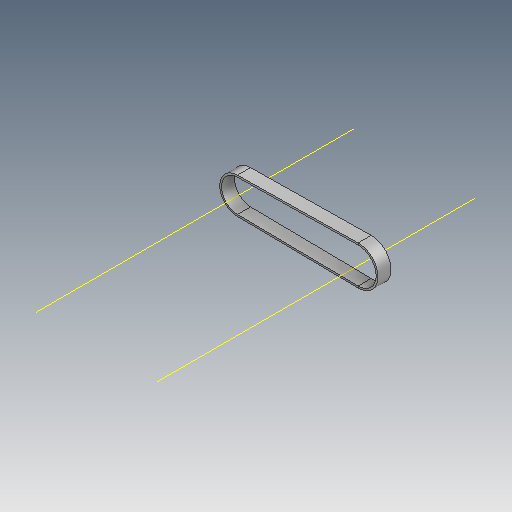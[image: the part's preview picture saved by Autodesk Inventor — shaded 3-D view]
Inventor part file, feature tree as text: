
AUTODESK INVENTOR PART (.ipt)
format: ipt  version: 2020.3 (Build 243373010, 373A)  size: 107,520 bytes
history: native  units: mm (DEFAULTED — no unit token found)
features: other x4, plane x2, sketch x1, sweep x1
ambient origin geometry x8: Origin, YZ Plane, XZ Plane, XY Plane, X Axis, Y Axis, Z Axis, Center Point
bodies: Solid1 (feature_tree)
feature tree (8):
  sketch  "Sketch Path"  dims[d0=12.0mm d2=0.0mm d4=0.381mm d5=1.27mm d6=0.0mm d7=0.0mm d8=0.0mm d9=0.0mm d10=0.0mm d11=0.0mm]
  other  "Cross Section Plane"
  other  "Work Axis1"
  other  "Work Axis2"
  plane  "Work Plane2"
  plane  "Work Plane3"
  sweep  "Belt"
  other  "Cross Section"
